# Revit family: CS5A
name_source: partatom
category: Generic Models
revit_build: Autodesk Revit LT 2017 (Build: 20160225_1515(x64)
units: mm (PartAtom-declared; Revit-internal decimal feet)

## family parameters
Always vertical = No
Can host rebar = No
Cut with Voids When Loaded = No
Part Type = Normal
Room Calculation Point = No
Round Connector Dimension = Use Diameter
Shared = No
Work Plane-Based = Yes

## types (1)
- NBS Standard Parameters
    BIMObjectName = Metpro_metprolibrary_electricalconnectionbox_connectorstrip_polyproplene
    Default Elevation = 1219 mm
    Description = CS5A -60Amp 12 way Connector Strip
    DurationUnit = year
    Finish = Natural
    Keynote = Max Temperature 80 degree celsius
    ManufacturerName = Metpro Ltd
    ManufacturerURL = www.metpro.co.uk
    Material = Polyethylene
    ModelReference = CS5A
    NBSDescription = Electrical Connection Boxes
    NBSReference = 90-60-25/485
    NominalHeight = 19 mm  [stored 0.062336 ft]
    NominalLength = 109 mm  [stored 0.357612 ft]
    NominalWidth = 16 mm
    ProductInformation = www.metpro.co.uk/pdf/cs5a.pdf
    Shape = Rectangular
    Size = 5 amp
    Uniclass2 = Pr_65_72_97_27
    Version = 1
    WarrantyDurationUnit = 1 year
    Weight = 0.02Kg

note: [stored X ft] marks values corroborated as IEEE doubles in the binary element streams (Revit-internal decimal feet)

## geometry (parser evidence)
native form markers: Sweep x2
no freeform markers — native parametric forms only
